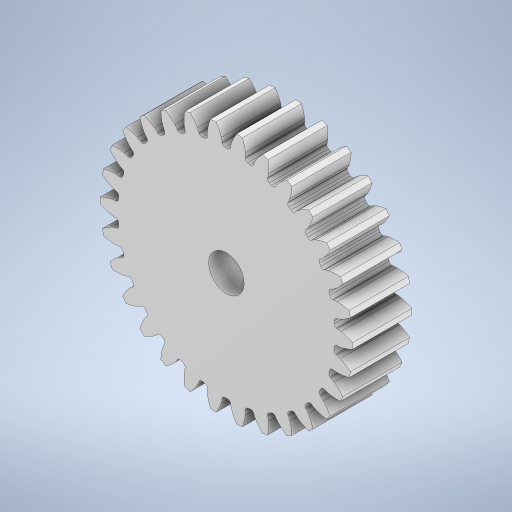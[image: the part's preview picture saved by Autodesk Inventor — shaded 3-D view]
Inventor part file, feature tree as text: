
AUTODESK INVENTOR PART (.ipt)
format: ipt  version: 2023 (Build 270158000, 158)  size: 594,432 bytes
history: native  units: in
note: dims shown in document units (in); Inventor stores cm internally (conversion verified against a paired STEP export)
features: extrude x1, sketch x1
ambient origin geometry x8: Origin, YZ Plane, XZ Plane, XY Plane, X Axis, Y Axis, Z Axis, Center Point
bodies: Solid1 (feature_tree)
feature tree (2):
  extrude  "Extrusion1"  Depth=0.3937in TaperAngle=0.0deg
  sketch  "Sketch1"  dims[d0=0.2362in d1=0.3937in d2=0.0in]
